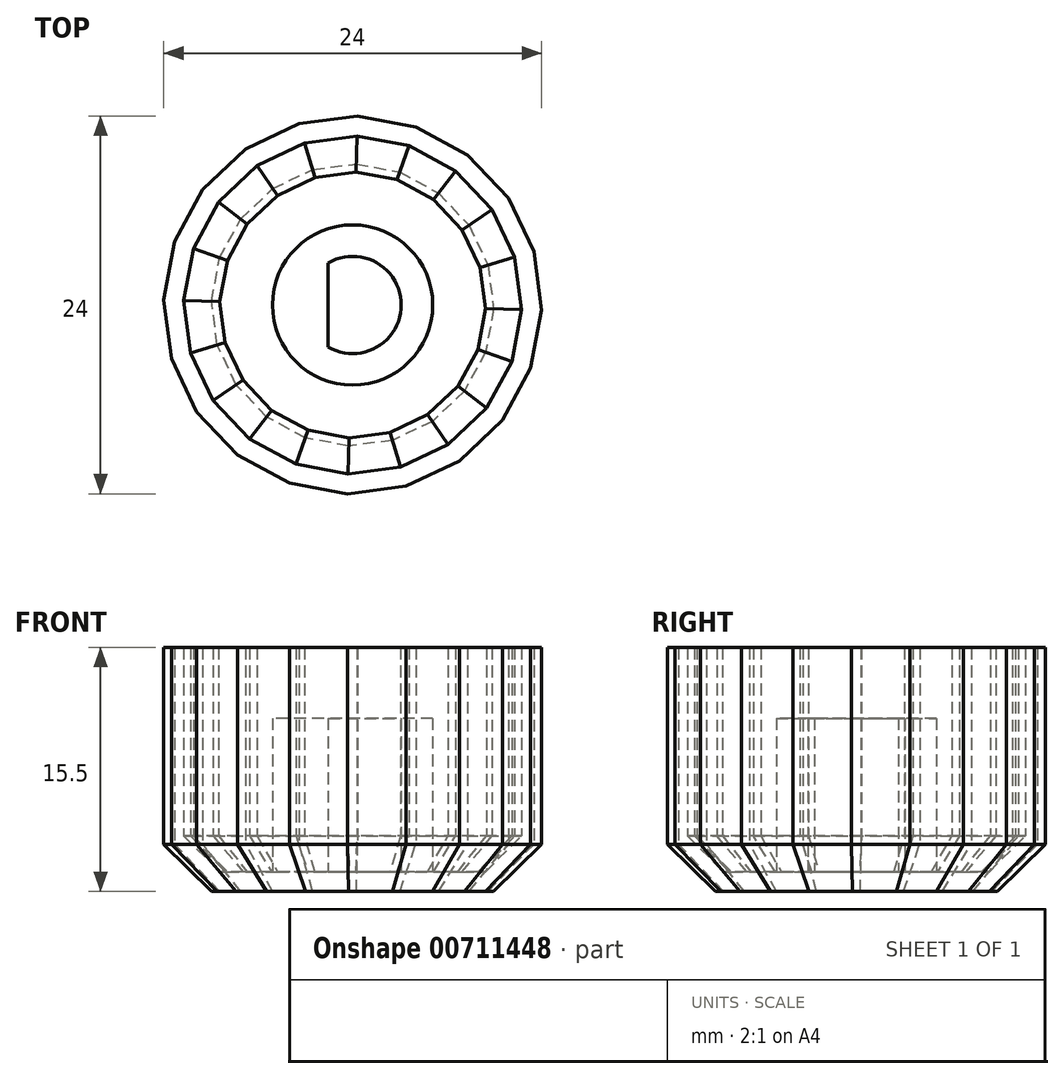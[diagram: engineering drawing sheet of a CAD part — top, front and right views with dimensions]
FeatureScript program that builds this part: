
annotation { "Feature Type Name" : "Feature", "Feature Type Description" : "" }
export const myFeature = defineFeature(function(context is Context, id is Id, definition is map)
    precondition{}
    {
        {
            var Q0;
            Q0=qCreatedBy(makeId("Top.planeOp"),FACE);
            var sketch = newSketch(context, id + "F0", { "sketchPlane" : qUnion([Q0])});
            skCircle(sketch, "E0.cCircle", {"center": v(0, 0) * mm, "radius": 12 * mm, "construction": true});
            skLineSegment(sketch, "E0.0", {"start": v(11.3, -4.02) * mm, "end": v(9.51, -7.32) * mm});
            skLineSegment(sketch, "E0.1", {"start": v(9.51, -7.32) * mm, "end": v(6.79, -9.9) * mm});
            skLineSegment(sketch, "E0.2", {"start": v(6.79, -9.9) * mm, "end": v(3.4, -11.5) * mm});
            skLineSegment(sketch, "E0.3", {"start": v(3.4, -11.5) * mm, "end": v(-0.33, -12) * mm});
            skLineSegment(sketch, "E0.4", {"start": v(-0.33, -12) * mm, "end": v(-4.02, -11.3) * mm});
            skLineSegment(sketch, "E0.5", {"start": v(-4.02, -11.3) * mm, "end": v(-7.32, -9.51) * mm});
            skLineSegment(sketch, "E0.6", {"start": v(-7.32, -9.51) * mm, "end": v(-9.9, -6.79) * mm});
            skLineSegment(sketch, "E0.7", {"start": v(-9.9, -6.79) * mm, "end": v(-11.5, -3.4) * mm});
            skLineSegment(sketch, "E0.8", {"start": v(-11.5, -3.4) * mm, "end": v(-12, 0.33) * mm});
            skLineSegment(sketch, "E0.9", {"start": v(-12, 0.33) * mm, "end": v(-11.3, 4.02) * mm});
            skLineSegment(sketch, "E0.10", {"start": v(-11.3, 4.02) * mm, "end": v(-9.51, 7.32) * mm});
            skLineSegment(sketch, "E0.11", {"start": v(-9.51, 7.32) * mm, "end": v(-6.79, 9.9) * mm});
            skLineSegment(sketch, "E0.12", {"start": v(-6.79, 9.9) * mm, "end": v(-3.4, 11.5) * mm});
            skLineSegment(sketch, "E0.13", {"start": v(-3.4, 11.5) * mm, "end": v(0.33, 12) * mm});
            skLineSegment(sketch, "E0.14", {"start": v(0.33, 12) * mm, "end": v(4.02, 11.3) * mm});
            skLineSegment(sketch, "E0.15", {"start": v(4.02, 11.3) * mm, "end": v(7.32, 9.51) * mm});
            skLineSegment(sketch, "E0.16", {"start": v(7.32, 9.51) * mm, "end": v(9.9, 6.79) * mm});
            skLineSegment(sketch, "E0.17", {"start": v(9.9, 6.79) * mm, "end": v(11.5, 3.4) * mm});
            skLineSegment(sketch, "E0.18", {"start": v(11.5, 3.4) * mm, "end": v(12, -0.33) * mm});
            skLineSegment(sketch, "E0.19", {"start": v(12, -0.33) * mm, "end": v(11.3, -4.02) * mm});
            skArc(sketch, "E1", {"start": v(-1.55, -2.68) * mm, "mid": v(3.09, 0) * mm, "end": v(-1.55, 2.68) * mm});
            skLineSegment(sketch, "E2", {"start": v(-1.55, 2.68) * mm, "end": v(-1.55, -2.68) * mm});
            skArc(sketch, "E3.0", {"start": v(-3.54, -3.65) * mm, "mid": v(5.1, 0) * mm, "end": v(-3.54, 3.65) * mm});
            skLineSegment(sketch, "E3.1", {"start": v(-3.55, 3.65) * mm, "end": v(-3.55, -3.65) * mm});
            skArc(sketch, "E4", {"start": v(-3.55, 3.65) * mm, "mid": v(-5.1, 0) * mm, "end": v(-3.55, -3.65) * mm});
            skPoint(sketch, "E5", {"position": v(3.09, 0) * mm});
            skSolve(sketch);
        }
        {
            var Q0;
            Q0=makeQuery(id+"F0.imprint","IMPRINT",FACE,{"disambiguationData":[TD([[makeQuery(id+"F0.imprint","IMPRINT",EDGE,{"derivedFrom":sQuery(id+"F0.wireOp",EDGE,"E0.0")}),-1.0]])]});
            var Q1;
            Q1=makeQuery(id+"F0.imprint","IMPRINT",FACE,{"disambiguationData":[TD([[makeQuery(id+"F0.imprint","IMPRINT",EDGE,{"derivedFrom":sQuery(id+"F0.wireOp",EDGE,"E1")}),-1.0]])]});
            var Q2;
            Q2=makeQuery(id+"F0.imprint","IMPRINT",FACE,{"disambiguationData":[TD([[makeQuery(id+"F0.imprint","IMPRINT",EDGE,{"derivedFrom":sQuery(id+"F0.wireOp",EDGE,"E1")}),1.0]])]});
            var Q3;
            Q3=makeQuery(id+"F0.imprint","IMPRINT",FACE,{"disambiguationData":[TD([[makeQuery(id+"F0.imprint","IMPRINT",EDGE,{"derivedFrom":sQuery(id+"F0.wireOp",EDGE,"E3.1")}),-1.0]])]});
            extrude(context, id + "F1", {"entities" : qUnion([Q0, Q1, Q2, Q3]), "depth" : 15.5 * mm, "offsetDistance" : 25 * mm});
        }
        {
            var Q0;
            Q0=makeQuery(id+"F1.opExtrude","CAP_FACE",FACE,{"disambiguationData":[OSD([sQuery(id+"F0.wireOp",EDGE,"E0.0"),sQuery(id+"F0.wireOp",EDGE,"E0.1"),sQuery(id+"F0.wireOp",EDGE,"E0.2"),sQuery(id+"F0.wireOp",EDGE,"E0.3"),sQuery(id+"F0.wireOp",EDGE,"E0.4"),sQuery(id+"F0.wireOp",EDGE,"E0.5"),sQuery(id+"F0.wireOp",EDGE,"E0.6"),sQuery(id+"F0.wireOp",EDGE,"E0.7"),sQuery(id+"F0.wireOp",EDGE,"E0.8"),sQuery(id+"F0.wireOp",EDGE,"E0.9"),sQuery(id+"F0.wireOp",EDGE,"E0.10"),sQuery(id+"F0.wireOp",EDGE,"E0.11"),sQuery(id+"F0.wireOp",EDGE,"E0.12"),sQuery(id+"F0.wireOp",EDGE,"E0.13"),sQuery(id+"F0.wireOp",EDGE,"E0.14"),sQuery(id+"F0.wireOp",EDGE,"E0.15"),sQuery(id+"F0.wireOp",EDGE,"E0.16"),sQuery(id+"F0.wireOp",EDGE,"E0.17"),sQuery(id+"F0.wireOp",EDGE,"E0.18"),sQuery(id+"F0.wireOp",EDGE,"E0.19")])],"isStart":true});
            chamfer(context, id + "F2", {"entities" : qUnion([Q0]), "width" : 3 * mm, "tangentPropagation" : true});
        }
        {
            var Q0;
            Q0=makeQuery(id+"F1.opExtrude","CAP_FACE",FACE,{"disambiguationData":[OSD([sQuery(id+"F0.wireOp",EDGE,"E0.0"),sQuery(id+"F0.wireOp",EDGE,"E0.1"),sQuery(id+"F0.wireOp",EDGE,"E0.2"),sQuery(id+"F0.wireOp",EDGE,"E0.3"),sQuery(id+"F0.wireOp",EDGE,"E0.4"),sQuery(id+"F0.wireOp",EDGE,"E0.5"),sQuery(id+"F0.wireOp",EDGE,"E0.6"),sQuery(id+"F0.wireOp",EDGE,"E0.7"),sQuery(id+"F0.wireOp",EDGE,"E0.8"),sQuery(id+"F0.wireOp",EDGE,"E0.9"),sQuery(id+"F0.wireOp",EDGE,"E0.10"),sQuery(id+"F0.wireOp",EDGE,"E0.11"),sQuery(id+"F0.wireOp",EDGE,"E0.12"),sQuery(id+"F0.wireOp",EDGE,"E0.13"),sQuery(id+"F0.wireOp",EDGE,"E0.14"),sQuery(id+"F0.wireOp",EDGE,"E0.15"),sQuery(id+"F0.wireOp",EDGE,"E0.16"),sQuery(id+"F0.wireOp",EDGE,"E0.17"),sQuery(id+"F0.wireOp",EDGE,"E0.18"),sQuery(id+"F0.wireOp",EDGE,"E0.19")])],"isStart":false});
            shell(context, id + "F3", {"entities" : qUnion([Q0]), "thickness" : 1.25 * mm});
        }
        {
            var Q0;
            Q0=makeQuery(id+"F0.imprint","IMPRINT",FACE,{"disambiguationData":[TD([[makeQuery(id+"F0.imprint","IMPRINT",EDGE,{"derivedFrom":sQuery(id+"F0.wireOp",EDGE,"E1")}),-1.0]])]});
            var Q1;
            Q1=makeQuery(id+"F0.imprint","IMPRINT",FACE,{"disambiguationData":[TD([[makeQuery(id+"F0.imprint","IMPRINT",EDGE,{"derivedFrom":sQuery(id+"F0.wireOp",EDGE,"E3.1")}),-1.0]])]});
            extrude(context, id + "F4", {"entities" : qUnion([Q0, Q1]), "operationType" : NewBodyOperationType.ADD, "depth" : 11 * mm, "offsetDistance" : 25 * mm});
        }
    });
